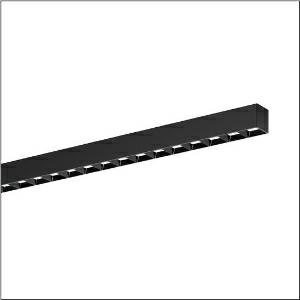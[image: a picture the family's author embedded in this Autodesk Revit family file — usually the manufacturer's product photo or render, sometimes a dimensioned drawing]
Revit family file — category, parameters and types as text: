
# Revit family: silica_r__21_51mx22dj33bb_1ad4
name_source: partatom
category: Lighting Fixtures
units: mm (PartAtom-declared; Revit-internal decimal feet)

## family parameters
Cut with Voids When Loaded = No
Host = Face
Light Source = No
Part Type = Normal
Room Calculation Point = No
Round Connector Dimension = Use Diameter
Shared = No

## types (1)
- --- (1 x LED, 3240 lm, 21.5 W, 3000K)
    Apparent Load = 22 VA
    CIE Flux Codes = 86 100 100 100 100
    Color Rendering = 80
    Color Temperature = 3000K
    Default Elevation = 1800 mm
    Description = Silica® 21, office luminaire, primary light control with darklight reflector, of PMMA, black, CAT 2 (L<= 3000cd/m²), light emission: direct distribution, primary light characteristic: symmetric, installation type: surface-mounted, LED, rated luminous flux: 3.240lm, luminous efficacy: 151lm/W, light colour: 830, colour temperature: 3000K, control gear: DALI 2, with terminal, 3+2-pole, max. 2.5mm², mains connection: 220..240V, AC, 50/60Hz, rated input power: 21.5W, luminaire housing, of aluminium, matt jet black (RAL 9005), length: 900mm, width: 53mm, height: 53mm, protection rating (complete): IP20, insulation class (complete): insulation class I (protective earthing), certification: CE, permissible operating ambient temperature: 0..+35°C, standard: EN 50419, packaging unit: 1 piece
    Height = 53 mm
    Lamp = 1 x LED
    Lamp Light Flux = 3240 lm
    Lamp Power = 21.5 W
    Lamp count = 1
    Length = 904 mm
    Luminous efficacy = 151 lm/W
    Manufacturer = Siteco
    ModVariant = No
    Model = 51MX22DJ33BB
    Mounting Place = Ceiling
    Mounting Type = Surface mounted
    Number of Poles = 1
    OnlyDefault = Yes
    Power Factor = 1
    Product Name = Silica® 21
    Product group = office luminaire | ceiling mounted
    ProductGroupID = 303
    Protection Class = Protection class I
    Protection Degree = IP 20
    RLX_Detail_Level = 1
    RLX_Emergency_Light_Flux = 0 lm
    RLX_Emergency_Type = 0
    RLX_Emergency_Type_DB = No
    RlxData = <blob elided: 21585 chars, md5=bce13cf7>
    Socket = socket
    Standby Power = 0 W
    System Light Flux = 3240 lm
    System Power = 22 W
    Type Comments = factory setting: luminous flux: 100 % | dim-lin: 254 | 195 mA
    Type Image = l_1335908.jpg
    URL = http://relux.com
    VarID = @adj_029939
    Voltage = 0 V
    Weight = 0.00 kg
    Width = 53 mm

## geometry (parser evidence)
native form markers: Blend x4, Sweep x12
no freeform markers — native parametric forms only
